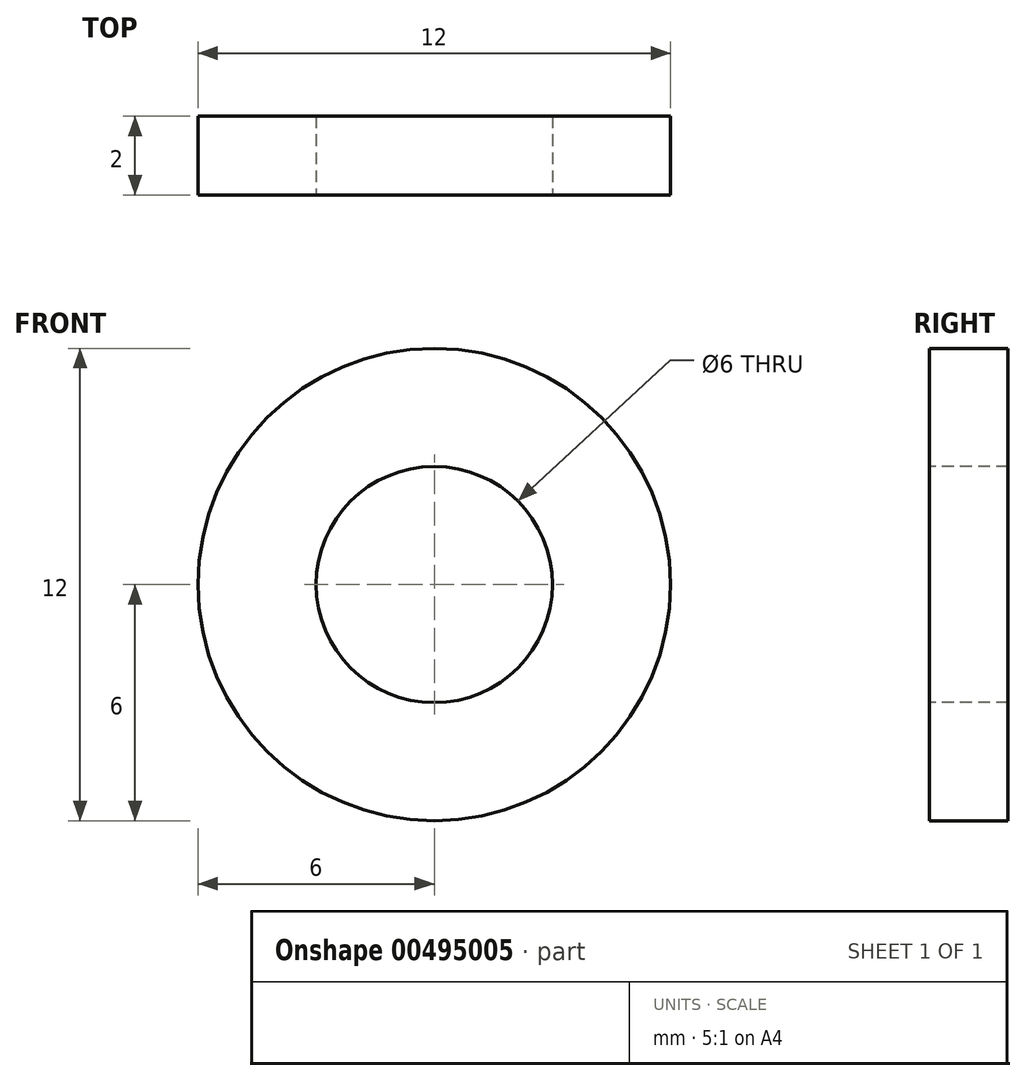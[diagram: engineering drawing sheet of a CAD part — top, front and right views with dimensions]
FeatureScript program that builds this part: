
annotation { "Feature Type Name" : "Feature", "Feature Type Description" : "" }
export const myFeature = defineFeature(function(context is Context, id is Id, definition is map)
    precondition{}
    {
        {
            var Q0;
            Q0=qCreatedBy(makeId("Front.planeOp"),FACE);
            var sketch = newSketch(context, id + "F0", { "sketchPlane" : qUnion([Q0])});
            skCircle(sketch, "E0", {"center": v(0, 0) * mm, "radius": 3 * mm});
            skCircle(sketch, "E1", {"center": v(0, 0) * mm, "radius": 6 * mm});
            skSolve(sketch);
        }
        {
            var Q0;
            Q0=makeQuery(id+"F0.imprint","IMPRINT",FACE,{"disambiguationData":[TD([[makeQuery(id+"F0.imprint","IMPRINT",EDGE,{"derivedFrom":sQuery(id+"F0.wireOp",EDGE,"E0")}),-1.0]])]});
            extrude(context, id + "F1", {"entities" : qUnion([Q0]), "oppositeDirection" : true, "depth" : 2 * mm});
        }
    });
